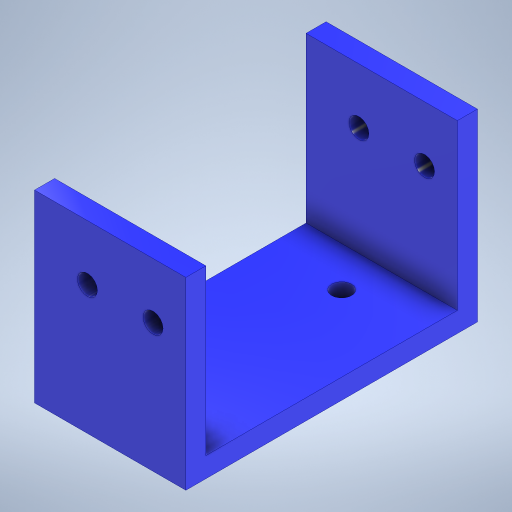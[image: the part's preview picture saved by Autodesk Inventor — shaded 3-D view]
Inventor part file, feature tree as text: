
AUTODESK INVENTOR PART (.ipt)
format: ipt  version: 2023 (Build 270158000, 158)  size: 299,008 bytes
history: native  units: mm
features: extrude x3, sketch x3
ambient origin geometry x8: Origin, YZ Plane, XZ Plane, XY Plane, X Axis, Y Axis, Z Axis, Center Point
bodies: Solid1 (feature_tree)
feature tree (6):
  extrude  "Extrusion1"  Depth=20.0mm
  extrude  "Extrusion2"  Depth=26.0mm
  extrude  "Extrusion3"  Depth=10.0mm
  sketch  "Sketch1"  dims[d0=20.0mm d1=20.0mm]
  sketch  "Sketch2"  dims[d2=55.5mm d3=26.0mm]
  sketch  "Sketch3"  dims[d5=20.0mm d6=45.5mm d7=20.0mm d8=10.0mm d9=10.0mm d10=26.0mm d11=75.5mm d12=0.0mm d13=75.5mm d14=0.0mm d21=65.5mm d22=55.5mm d23=10.0mm d24=10.0mm d25=0.0mm d26=0.0mm]
